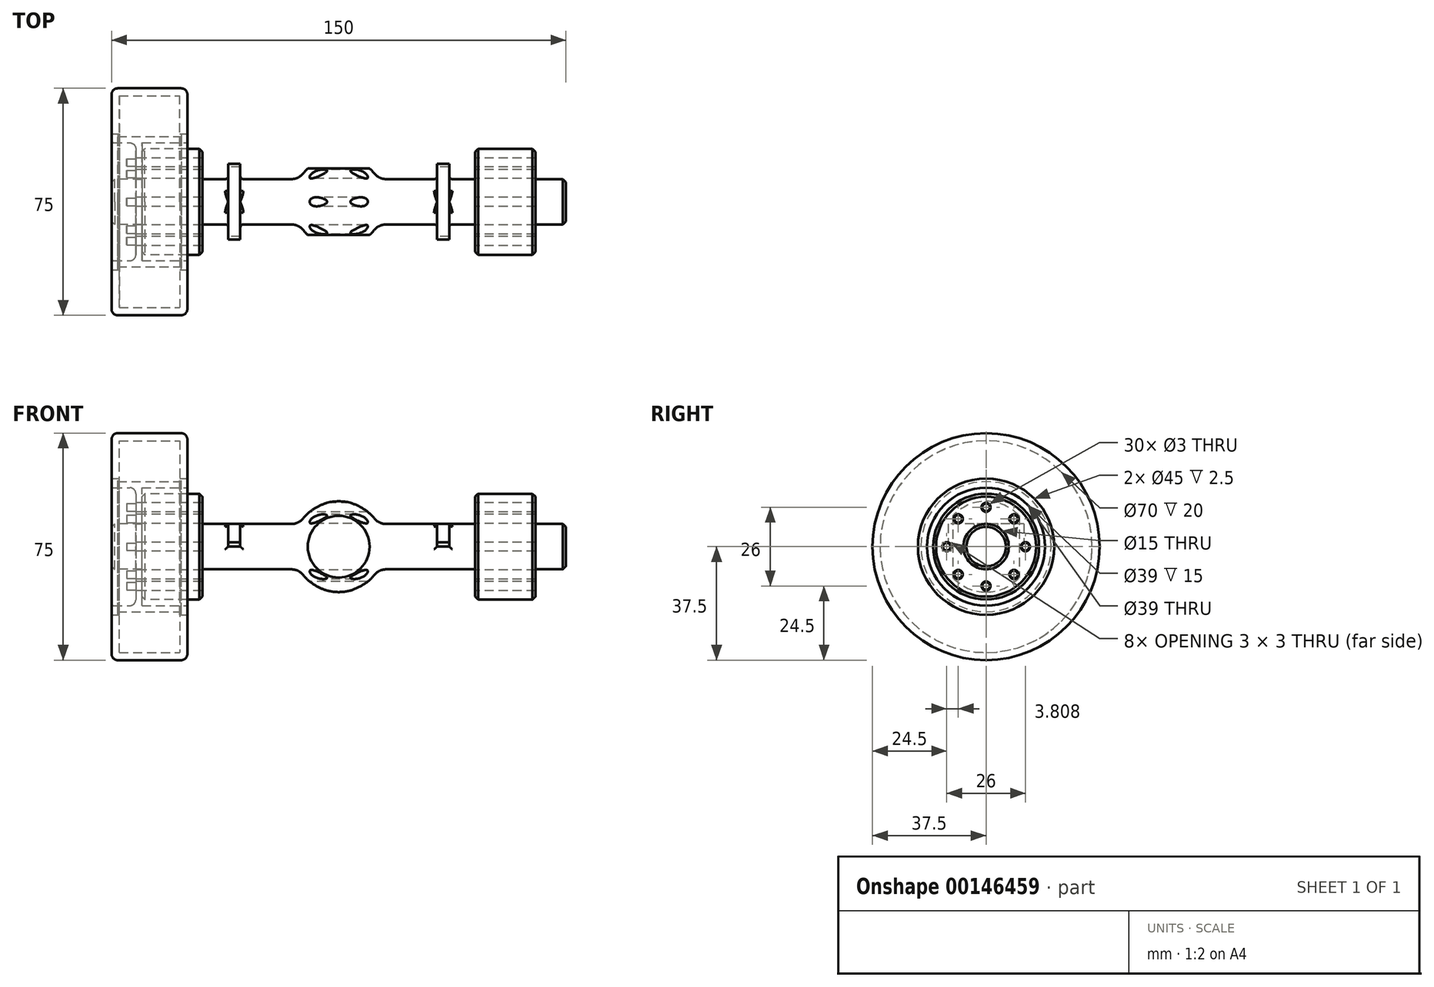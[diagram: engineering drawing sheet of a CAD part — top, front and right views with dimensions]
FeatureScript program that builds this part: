
annotation { "Feature Type Name" : "Feature", "Feature Type Description" : "" }
export const myFeature = defineFeature(function(context is Context, id is Id, definition is map)
    precondition{}
    {
        {
            var Q0;
            Q0=qCreatedBy(makeId("Front.planeOp"),FACE);
            var sketch = newSketch(context, id + "F0", { "sketchPlane" : qUnion([Q0])});
            skLineSegment(sketch, "E0", {"start": v(-13, 7.5) * mm, "end": v(-45, 7.5) * mm});
            skLineSegment(sketch, "E1", {"start": v(-45, 7.5) * mm, "end": v(-45, 17.5) * mm});
            skLineSegment(sketch, "E2", {"start": v(-45, 17.5) * mm, "end": v(-65, 17.5) * mm});
            skLineSegment(sketch, "E3", {"start": v(-65, 17.5) * mm, "end": v(-65, 7.5) * mm});
            skLineSegment(sketch, "E4", {"start": v(-65, 7.5) * mm, "end": v(-75, 7.5) * mm});
            skLineSegment(sketch, "E5", {"start": v(-75, 7.5) * mm, "end": v(-75, 0) * mm});
            skLineSegment(sketch, "E6", {"start": v(0, 0) * mm, "end": v(0, 15) * mm});
            skArc(sketch, "E7", {"start": v(0, 15) * mm, "mid": v(-7.5, 13) * mm, "end": v(-13, 7.5) * mm});
            skLineSegment(sketch, "E8", {"start": v(-75, 0) * mm, "end": v(0, 0) * mm});
            skLineSegment(sketch, "E9", {"start": v(0, 0) * mm, "end": v(14.2, 0) * mm, "construction": true});
            skSolve(sketch);
        }
        {
            var Q0;
            Q0 = qSketchRegion(id + "F0", true);
            var Q1;
            Q1=sQuery(id+"F0.wireOp",EDGE,"E9");
            revolve(context, id + "F1", {"entities" : qUnion([Q0]), "axis" : qUnion([Q1]), "revolveType" : RevolveType.FULL});
        }
        {
            var Q0;
            Q0=qCreatedBy(makeId("Top.planeOp"),FACE);
            var sketch = newSketch(context, id + "F2", { "sketchPlane" : qUnion([Q0])});
            skLineSegment(sketch, "E10.bottom", {"start": v(-16.82, 17.7) * mm, "end": v(18.57, 17.7) * mm});
            skLineSegment(sketch, "E10.top", {"start": v(-16.82, 11) * mm, "end": v(18.57, 11) * mm});
            skLineSegment(sketch, "E10.left", {"start": v(-16.82, 17.7) * mm, "end": v(-16.82, 11) * mm});
            skLineSegment(sketch, "E10.right", {"start": v(18.57, 17.7) * mm, "end": v(18.57, 11) * mm});
            skLineSegment(sketch, "E11.bottom", {"start": v(-18.74, -20.13) * mm, "end": v(18.51, -20.13) * mm});
            skLineSegment(sketch, "E11.top", {"start": v(-18.74, -11) * mm, "end": v(18.51, -11) * mm});
            skLineSegment(sketch, "E11.left", {"start": v(-18.74, -20.13) * mm, "end": v(-18.74, -11) * mm});
            skLineSegment(sketch, "E11.right", {"start": v(18.51, -20.13) * mm, "end": v(18.51, -11) * mm});
            skSolve(sketch);
        }
        {
            var Q0;
            Q0 = qSketchRegion(id + "F2", true);
            extrude(context, id + "F3", {"entities" : qUnion([Q0]), "operationType" : NewBodyOperationType.REMOVE, "depth" : 50 * mm, "symmetric" : true});
        }
        {
            var Q0;
            Q0=makeQuery(id+"F1.opRevolve","SWEPT_EDGE",EDGE,{"disambiguationData":[OSD([sQuery(id+"F0.wireOp",EDGE,"E4"),sQuery(id+"F0.wireOp",EDGE,"E5")])]});
            var Q1;
            Q1=makeQuery(id+"F1.opRevolve","SWEPT_EDGE",EDGE,{"disambiguationData":[OSD([sQuery(id+"F0.wireOp",EDGE,"E2"),sQuery(id+"F0.wireOp",EDGE,"E3")])]});
            var Q2;
            Q2=makeQuery(id+"F1.opRevolve","SWEPT_EDGE",EDGE,{"disambiguationData":[OSD([sQuery(id+"F0.wireOp",EDGE,"E1"),sQuery(id+"F0.wireOp",EDGE,"E2")])]});
            var Q3;
            Q3=makeQuery(id+"FlIVTg58INy0Y5d_1.opPattern","COPY",EDGE,{"derivedFrom":makeQuery(id+"F1.opRevolve","SWEPT_EDGE",EDGE,{"disambiguationData":[OSD([sQuery(id+"F0.wireOp",EDGE,"E1"),sQuery(id+"F0.wireOp",EDGE,"E2")])]}),"instanceName":"1"});
            var Q4;
            Q4=makeQuery(id+"FlIVTg58INy0Y5d_1.opPattern","COPY",EDGE,{"derivedFrom":makeQuery(id+"F1.opRevolve","SWEPT_EDGE",EDGE,{"disambiguationData":[OSD([sQuery(id+"F0.wireOp",EDGE,"E2"),sQuery(id+"F0.wireOp",EDGE,"E3")])]}),"instanceName":"1"});
            var Q5;
            Q5=makeQuery(id+"FlIVTg58INy0Y5d_1.opPattern","COPY",EDGE,{"derivedFrom":makeQuery(id+"F1.opRevolve","SWEPT_EDGE",EDGE,{"disambiguationData":[OSD([sQuery(id+"F0.wireOp",EDGE,"E4"),sQuery(id+"F0.wireOp",EDGE,"E5")])]}),"instanceName":"1"});
            chamfer(context, id + "F4", {"entities" : qUnion([Q0, Q1, Q2, Q3, Q4, Q5]), "width" : 1 * mm, "tangentPropagation" : true});
        }
        {
            var Q0;
            Q0=qCreatedBy(makeId("Top.planeOp"),FACE);
            var sketch = newSketch(context, id + "F5", { "sketchPlane" : qUnion([Q0])});
            skLineSegment(sketch, "E12.bottom", {"start": v(-32.5, 12.5) * mm, "end": v(-36.5, 12.5) * mm});
            skLineSegment(sketch, "E12.top", {"start": v(-32.5, -12.5) * mm, "end": v(-36.5, -12.5) * mm});
            skLineSegment(sketch, "E12.left", {"start": v(-32.5, 12.5) * mm, "end": v(-32.5, -12.5) * mm});
            skLineSegment(sketch, "E12.right", {"start": v(-36.5, 12.5) * mm, "end": v(-36.5, -12.5) * mm});
            skPoint(sketch, "E12.middle", {"position": v(-34.5, 0) * mm});
            skLineSegment(sketch, "E13.bottom", {"start": v(36.5, 12.5) * mm, "end": v(32.5, 12.5) * mm, "construction": true});
            skLineSegment(sketch, "E13.top", {"start": v(36.5, -12.5) * mm, "end": v(32.5, -12.5) * mm, "construction": true});
            skLineSegment(sketch, "E13.left", {"start": v(36.5, 12.5) * mm, "end": v(36.5, -12.5) * mm, "construction": true});
            skLineSegment(sketch, "E13.right", {"start": v(32.5, 12.5) * mm, "end": v(32.5, -12.5) * mm, "construction": true});
            skPoint(sketch, "E13.middle", {"position": v(34.5, 0) * mm});
            skSolve(sketch);
        }
        {
            var Q0;
            Q0 = qSketchRegion(id + "F5", true);
            extrude(context, id + "F6", {"entities" : qUnion([Q0]), "operationType" : NewBodyOperationType.ADD, "depth" : 7.5 * mm});
        }
        {
            var Q0;
            Q0=makeQuery(id+"F1.opRevolve","SWEPT_EDGE",EDGE,{"disambiguationData":[OSD([sQuery(id+"F0.wireOp",EDGE,"E0"),sQuery(id+"F0.wireOp",EDGE,"E7")])]});
            var Q1;
            Q1=makeQuery(id+"FlIVTg58INy0Y5d_1.opPattern","COPY",EDGE,{"derivedFrom":makeQuery(id+"F1.opRevolve","SWEPT_EDGE",EDGE,{"disambiguationData":[OSD([sQuery(id+"F0.wireOp",EDGE,"E0"),sQuery(id+"F0.wireOp",EDGE,"E7")])]}),"instanceName":"1"});
            fillet(context, id + "F7", {"entities" : qUnion([Q0, Q1]), "radius" : 5 * mm, "tangentPropagation" : true, "allowEdgeOverflow" : false});
        }
        {
            var Q0;
            Q0=makeQuery(id+"F6.boolean.opBoolean","INTERSECT",EDGE,{"disambiguationData":[OD(1.0)],"derivedFrom":[makeQuery(id+"F1.opRevolve","SWEPT_FACE",FACE,{"disambiguationData":[OSD([sQuery(id+"F0.wireOp",EDGE,"E0")])]}),makeQuery(id+"F6.opExtrude","SWEPT_FACE",FACE,{"disambiguationData":[OSD([sQuery(id+"F5.wireOp",EDGE,"E12.right")])]})]});
            var Q1;
            Q1=makeQuery(id+"F6.boolean.opBoolean","INTERSECT",EDGE,{"disambiguationData":[OD(1.0)],"derivedFrom":[makeQuery(id+"F1.opRevolve","SWEPT_FACE",FACE,{"disambiguationData":[OSD([sQuery(id+"F0.wireOp",EDGE,"E0")])]}),makeQuery(id+"F6.opExtrude","SWEPT_FACE",FACE,{"disambiguationData":[OSD([sQuery(id+"F5.wireOp",EDGE,"E12.left")])]})]});
            var Q2;
            Q2=makeQuery(id+"F6.boolean.opBoolean","INTERSECT",EDGE,{"disambiguationData":[OD(1.0)],"derivedFrom":[makeQuery(id+"F1.opRevolve","SWEPT_FACE",FACE,{"disambiguationData":[OSD([sQuery(id+"F0.wireOp",EDGE,"E0")])]}),makeQuery(id+"F6.opExtrude","CAP_FACE",FACE,{"disambiguationData":[OSD([sQuery(id+"F5.wireOp",EDGE,"E12.bottom"),sQuery(id+"F5.wireOp",EDGE,"E12.top"),sQuery(id+"F5.wireOp",EDGE,"E12.left"),sQuery(id+"F5.wireOp",EDGE,"E12.right")])],"isStart":true})]});
            var Q3;
            Q3=makeQuery(id+"F6.boolean.opBoolean","INTERSECT",EDGE,{"disambiguationData":[OD(0.0)],"derivedFrom":[makeQuery(id+"F1.opRevolve","SWEPT_FACE",FACE,{"disambiguationData":[OSD([sQuery(id+"F0.wireOp",EDGE,"E0")])]}),makeQuery(id+"F6.opExtrude","CAP_FACE",FACE,{"disambiguationData":[OSD([sQuery(id+"F5.wireOp",EDGE,"E12.bottom"),sQuery(id+"F5.wireOp",EDGE,"E12.top"),sQuery(id+"F5.wireOp",EDGE,"E12.left"),sQuery(id+"F5.wireOp",EDGE,"E12.right")])],"isStart":true})]});
            fillet(context, id + "F8", {"entities" : qUnion([Q0, Q1, Q2, Q3]), "radius" : 1 * mm, "tangentPropagation" : true, "allowEdgeOverflow" : false});
        }
        {
            var Q0;
            Q0=makeQuery(id+"F1.opRevolve","SWEPT_FACE",FACE,{"disambiguationData":[OSD([sQuery(id+"F0.wireOp",EDGE,"E3")])]});
            var sketch = newSketch(context, id + "F9", { "sketchPlane" : qUnion([Q0])});
            skCircle(sketch, "E14", {"center": v(0, 13) * mm, "radius": 1.25 * mm});
            skCircle(sketch, "E15.1.0", {"center": v(-9.2, 9.2) * mm, "radius": 1.25 * mm});
            skCircle(sketch, "E15.2.0", {"center": v(-13, 0) * mm, "radius": 1.25 * mm});
            skCircle(sketch, "E15.3.0", {"center": v(-9.2, -9.2) * mm, "radius": 1.25 * mm});
            skCircle(sketch, "E15.4.0", {"center": v(0, -13) * mm, "radius": 1.25 * mm});
            skCircle(sketch, "E15.5.0", {"center": v(9.2, -9.2) * mm, "radius": 1.25 * mm});
            skCircle(sketch, "E15.6.0", {"center": v(13, 0) * mm, "radius": 1.25 * mm});
            skCircle(sketch, "E15.7.0", {"center": v(9.2, 9.2) * mm, "radius": 1.25 * mm});
            skPoint(sketch, "E15.center", {"position": v(0, 0) * mm});
            skSolve(sketch);
        }
        {
            var Q0;
            Q0 = qSketchRegion(id + "F9", true);
            extrude(context, id + "F10", {"entities" : qUnion([Q0]), "operationType" : NewBodyOperationType.ADD, "depth" : 5 * mm});
        }
        {
            var Q0;
            Q0=makeQuery(id+"F1.opRevolve","SWEPT_BODY",BODY,{"disambiguationData":[OSD([sQuery(id+"F0.wireOp",EDGE,"E0"),sQuery(id+"F0.wireOp",EDGE,"E1"),sQuery(id+"F0.wireOp",EDGE,"E2"),sQuery(id+"F0.wireOp",EDGE,"E3"),sQuery(id+"F0.wireOp",EDGE,"E4"),sQuery(id+"F0.wireOp",EDGE,"E5"),sQuery(id+"F0.wireOp",EDGE,"E6"),sQuery(id+"F0.wireOp",EDGE,"E7"),sQuery(id+"F0.wireOp",EDGE,"E8")])]});
            var Q1;
            Q1=qCreatedBy(makeId("Right.planeOp"),FACE);
            mirror(context, id + "F11", {"operationType" : NewBodyOperationType.ADD, "entities" : qUnion([Q0]), "mirrorPlane" : qUnion([Q1])});
        }
        {
            var Q0;
            Q0=qCreatedBy(makeId("Front.planeOp"),FACE);
            var sketch = newSketch(context, id + "F12", { "sketchPlane" : qUnion([Q0])});
            skLineSegment(sketch, "E16", {"start": v(-67, 7.5) * mm, "end": v(-65, 7.5) * mm});
            skLineSegment(sketch, "E17", {"start": v(-65, 7.5) * mm, "end": v(-65, 19.5) * mm});
            skLineSegment(sketch, "E18", {"start": v(-65, 19.5) * mm, "end": v(-50, 19.5) * mm});
            skLineSegment(sketch, "E19", {"start": v(-50, 19.5) * mm, "end": v(-50, 22.5) * mm});
            skLineSegment(sketch, "E20", {"start": v(-50, 22.5) * mm, "end": v(-52, 22.5) * mm});
            skLineSegment(sketch, "E21", {"start": v(-75, 22.5) * mm, "end": v(-75, 19.5) * mm});
            skLineSegment(sketch, "E22", {"start": v(-75, 19.5) * mm, "end": v(-67, 19.5) * mm});
            skLineSegment(sketch, "E23", {"start": v(-67, 19.5) * mm, "end": v(-67, 7.5) * mm});
            skLineSegment(sketch, "E24", {"start": v(0, 0) * mm, "end": v(-95.44, 0) * mm, "construction": true});
            skLineSegment(sketch, "E25", {"start": v(-73, 22.5) * mm, "end": v(-73, 21.5) * mm});
            skLineSegment(sketch, "E26", {"start": v(-73, 21.5) * mm, "end": v(-52, 21.5) * mm});
            skLineSegment(sketch, "E27", {"start": v(-52, 21.5) * mm, "end": v(-52, 22.5) * mm});
            skLineSegment(sketch, "E28.trimOffspring", {"start": v(-73, 22.5) * mm, "end": v(-75, 22.5) * mm});
            skSolve(sketch);
        }
        {
            var Q0;
            Q0 = qSketchRegion(id + "F12", true);
            var Q1;
            Q1=sQuery(id+"F12.wireOp",EDGE,"E24");
            revolve(context, id + "F13", {"entities" : qUnion([Q0]), "axis" : qUnion([Q1]), "revolveType" : RevolveType.FULL});
        }
        {
            var Q0;
            Q0=makeQuery(id+"F13.opRevolve","SWEPT_FACE",FACE,{"disambiguationData":[OSD([sQuery(id+"F12.wireOp",EDGE,"E23")])]});
            var sketch = newSketch(context, id + "F14", { "sketchPlane" : qUnion([Q0])});
            skCircle(sketch, "E29.0", {"center": v(0, 13) * mm, "radius": 1.25 * mm, "construction": true});
            skCircle(sketch, "E30", {"center": v(0, 13) * mm, "radius": 1.5 * mm});
            skCircle(sketch, "E31.1.0", {"center": v(-9.2, 9.2) * mm, "radius": 1.5 * mm});
            skCircle(sketch, "E31.2.0", {"center": v(-13, 0) * mm, "radius": 1.5 * mm});
            skCircle(sketch, "E31.3.0", {"center": v(-9.2, -9.2) * mm, "radius": 1.5 * mm});
            skCircle(sketch, "E31.4.0", {"center": v(0, -13) * mm, "radius": 1.5 * mm});
            skCircle(sketch, "E31.5.0", {"center": v(9.2, -9.2) * mm, "radius": 1.5 * mm});
            skCircle(sketch, "E31.6.0", {"center": v(13, 0) * mm, "radius": 1.5 * mm});
            skCircle(sketch, "E31.7.0", {"center": v(9.2, 9.2) * mm, "radius": 1.5 * mm});
            skPoint(sketch, "E31.center", {"position": v(0, 0) * mm});
            skSolve(sketch);
        }
        {
            var Q0;
            Q0 = qSketchRegion(id + "F14", true);
            extrude(context, id + "F15", {"entities" : qUnion([Q0]), "operationType" : NewBodyOperationType.REMOVE, "endBound" : BoundingType.THROUGH_ALL, "oppositeDirection" : true, "depth" : 25 * mm});
        }
        {
            var Q0;
            Q0=makeQuery(id+"F13.opRevolve","SWEPT_EDGE",EDGE,{"disambiguationData":[OSD([sQuery(id+"F12.wireOp",EDGE,"E22"),sQuery(id+"F12.wireOp",EDGE,"E23")])]});
            fillet(context, id + "F16", {"entities" : qUnion([Q0]), "radius" : 2 * mm, "tangentPropagation" : true, "allowEdgeOverflow" : false});
        }
        {
            var Q0;
            Q0=makeQuery(id+"F13.opRevolve","SWEPT_EDGE",EDGE,{"disambiguationData":[OSD([sQuery(id+"F12.wireOp",EDGE,"E21"),sQuery(id+"F12.wireOp",EDGE,"E22")])]});
            fillet(context, id + "F17", {"entities" : qUnion([Q0]), "radius" : 0.5 * mm, "tangentPropagation" : true, "allowEdgeOverflow" : false});
        }
        {
            var Q0;
            Q0=qCreatedBy(makeId("Front.planeOp"),FACE);
            var sketch = newSketch(context, id + "F18", { "sketchPlane" : qUnion([Q0])});
            skLineSegment(sketch, "E32", {"start": v(-75, 22.5) * mm, "end": v(-50, 22.5) * mm});
            skLineSegment(sketch, "E33", {"start": v(-75, 22.5) * mm, "end": v(-75, 37.5) * mm});
            skLineSegment(sketch, "E34", {"start": v(-75, 37.5) * mm, "end": v(-50, 37.5) * mm});
            skLineSegment(sketch, "E35", {"start": v(-50, 37.5) * mm, "end": v(-50, 22.5) * mm});
            skLineSegment(sketch, "E36", {"start": v(0, 0) * mm, "end": v(-85.38, 0) * mm, "construction": true});
            skSolve(sketch);
        }
        {
            var Q0;
            Q0 = qSketchRegion(id + "F18", true);
            var Q1;
            Q1=sQuery(id+"F18.wireOp",EDGE,"E36");
            revolve(context, id + "F19", {"entities" : qUnion([Q0]), "axis" : qUnion([Q1]), "revolveType" : RevolveType.FULL});
        }
        {
            var Q0;
            Q0=makeQuery(id+"F19.opRevolve","SWEPT_EDGE",EDGE,{"disambiguationData":[OSD([sQuery(id+"F18.wireOp",EDGE,"E33"),sQuery(id+"F18.wireOp",EDGE,"E34")])]});
            var Q1;
            Q1=makeQuery(id+"F19.opRevolve","SWEPT_EDGE",EDGE,{"disambiguationData":[OSD([sQuery(id+"F18.wireOp",EDGE,"E34"),sQuery(id+"F18.wireOp",EDGE,"E35")])]});
            fillet(context, id + "F20", {"entities" : qUnion([Q0, Q1]), "radius" : 2 * mm, "tangentPropagation" : true, "allowEdgeOverflow" : false});
        }
        {
            var Q0;
            Q0=makeQuery(id+"F19.opRevolve","SWEPT_FACE",FACE,{"disambiguationData":[OSD([sQuery(id+"F18.wireOp",EDGE,"E32")])]});
            shell(context, id + "F21", {"entities" : qUnion([Q0]), "thickness" : 2.5 * mm});
        }
    });
